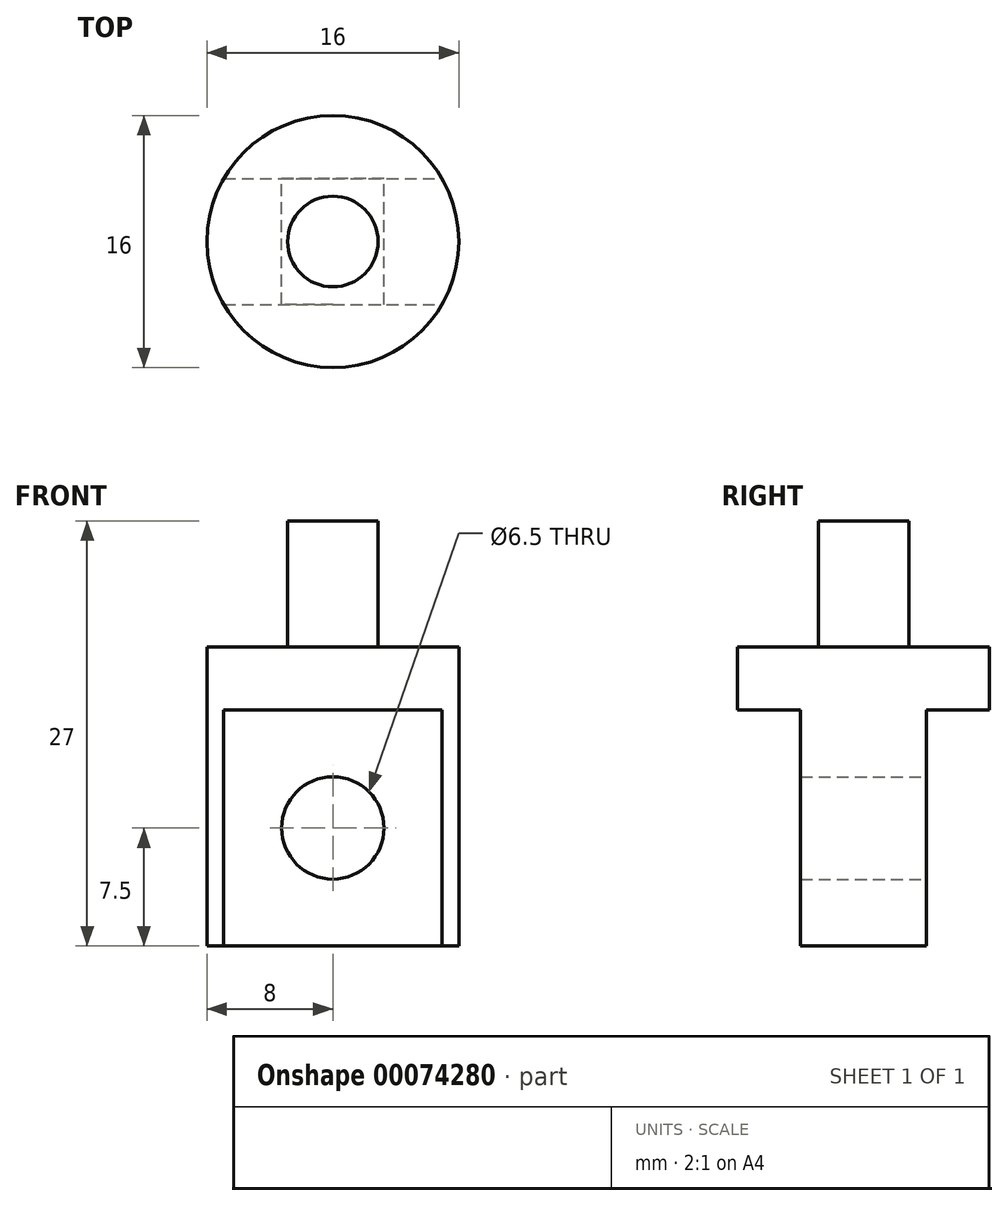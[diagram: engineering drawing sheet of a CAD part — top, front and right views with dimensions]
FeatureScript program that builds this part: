
annotation { "Feature Type Name" : "Feature", "Feature Type Description" : "" }
export const myFeature = defineFeature(function(context is Context, id is Id, definition is map)
    precondition{}
    {
        {
            var Q0;
            Q0=qCreatedBy(makeId("Top.planeOp"),FACE);
            var sketch = newSketch(context, id + "F0", { "sketchPlane" : qUnion([Q0])});
            skCircle(sketch, "E0", {"center": v(0, 0) * mm, "radius": 8 * mm});
            skCircle(sketch, "E1", {"center": v(0, 0) * mm, "radius": 2.88 * mm});
            skLineSegment(sketch, "E2", {"start": v(-6.93, 4) * mm, "end": v(6.93, 4) * mm});
            skLineSegment(sketch, "E3", {"start": v(-6.93, -4) * mm, "end": v(6.93, -4) * mm});
            skSolve(sketch);
        }
        {
            var Q0;
            Q0=makeQuery(id+"F0.imprint","IMPRINT",FACE,{"disambiguationData":[TD([[makeQuery(id+"F0.imprint","IMPRINT",EDGE,{"derivedFrom":sQuery(id+"F0.wireOp",EDGE,"E1")}),1.0]])]});
            extrude(context, id + "F1", {"entities" : qUnion([Q0]), "depth" : 8 * mm});
        }
        {
            var Q0;
            {var subQ0=sQuery(id+"F0.wireOp",EDGE,"E3");Q0=makeQuery(id+"F0.imprint","IMPRINT",FACE,{"disambiguationData":[TD([[makeQuery(id+"F0.imprint","IMPRINT",EDGE,{"derivedFrom":subQ0}),-1.0]])]});}
            var Q1;
            {var subQ0=sQuery(id+"F0.wireOp",EDGE,"E2");Q1=makeQuery(id+"F0.imprint","IMPRINT",FACE,{"disambiguationData":[TD([[makeQuery(id+"F0.imprint","IMPRINT",EDGE,{"derivedFrom":subQ0}),1.0]])]});}
            var Q2;
            Q2=makeQuery(id+"F0.imprint","IMPRINT",FACE,{"disambiguationData":[TD([[makeQuery(id+"F0.imprint","IMPRINT",EDGE,{"derivedFrom":sQuery(id+"F0.wireOp",EDGE,"E1")}),-1.0]])]});
            var Q3;
            Q3=makeQuery(id+"F0.imprint","IMPRINT",FACE,{"disambiguationData":[TD([[makeQuery(id+"F0.imprint","IMPRINT",EDGE,{"derivedFrom":sQuery(id+"F0.wireOp",EDGE,"E1")}),1.0]])]});
            extrude(context, id + "F2", {"entities" : qUnion([Q0, Q1, Q2, Q3]), "operationType" : NewBodyOperationType.ADD, "oppositeDirection" : true, "depth" : 4 * mm});
        }
        {
            var Q0;
            Q0=makeQuery(id+"F0.imprint","IMPRINT",FACE,{"disambiguationData":[TD([[makeQuery(id+"F0.imprint","IMPRINT",EDGE,{"derivedFrom":sQuery(id+"F0.wireOp",EDGE,"E1")}),-1.0]])]});
            var Q1;
            Q1=makeQuery(id+"F0.imprint","IMPRINT",FACE,{"disambiguationData":[TD([[makeQuery(id+"F0.imprint","IMPRINT",EDGE,{"derivedFrom":sQuery(id+"F0.wireOp",EDGE,"E1")}),1.0]])]});
            extrude(context, id + "F3", {"entities" : qUnion([Q0, Q1]), "operationType" : NewBodyOperationType.ADD, "oppositeDirection" : true, "depth" : 19 * mm});
        }
        {
            var Q0;
            Q0=makeQuery(id+"F3.opExtrude","SWEPT_FACE",FACE,{"disambiguationData":[OSD([sQuery(id+"F0.wireOp",EDGE,"E2")])]});
            var sketch = newSketch(context, id + "F4", { "sketchPlane" : qUnion([Q0])});
            skCircle(sketch, "E4", {"center": v(0, -11.5) * mm, "radius": 3.25 * mm});
            skSolve(sketch);
        }
        {
            var Q0;
            Q0=makeQuery(id+"F4.imprint","IMPRINT",FACE,{"disambiguationData":[TD([[makeQuery(id+"F4.imprint","IMPRINT",EDGE,{"derivedFrom":sQuery(id+"F4.wireOp",EDGE,"E4")}),1.0]])]});
            extrude(context, id + "F5", {"entities" : qUnion([Q0]), "operationType" : NewBodyOperationType.REMOVE, "oppositeDirection" : true, "depth" : 25 * mm});
        }
    });
